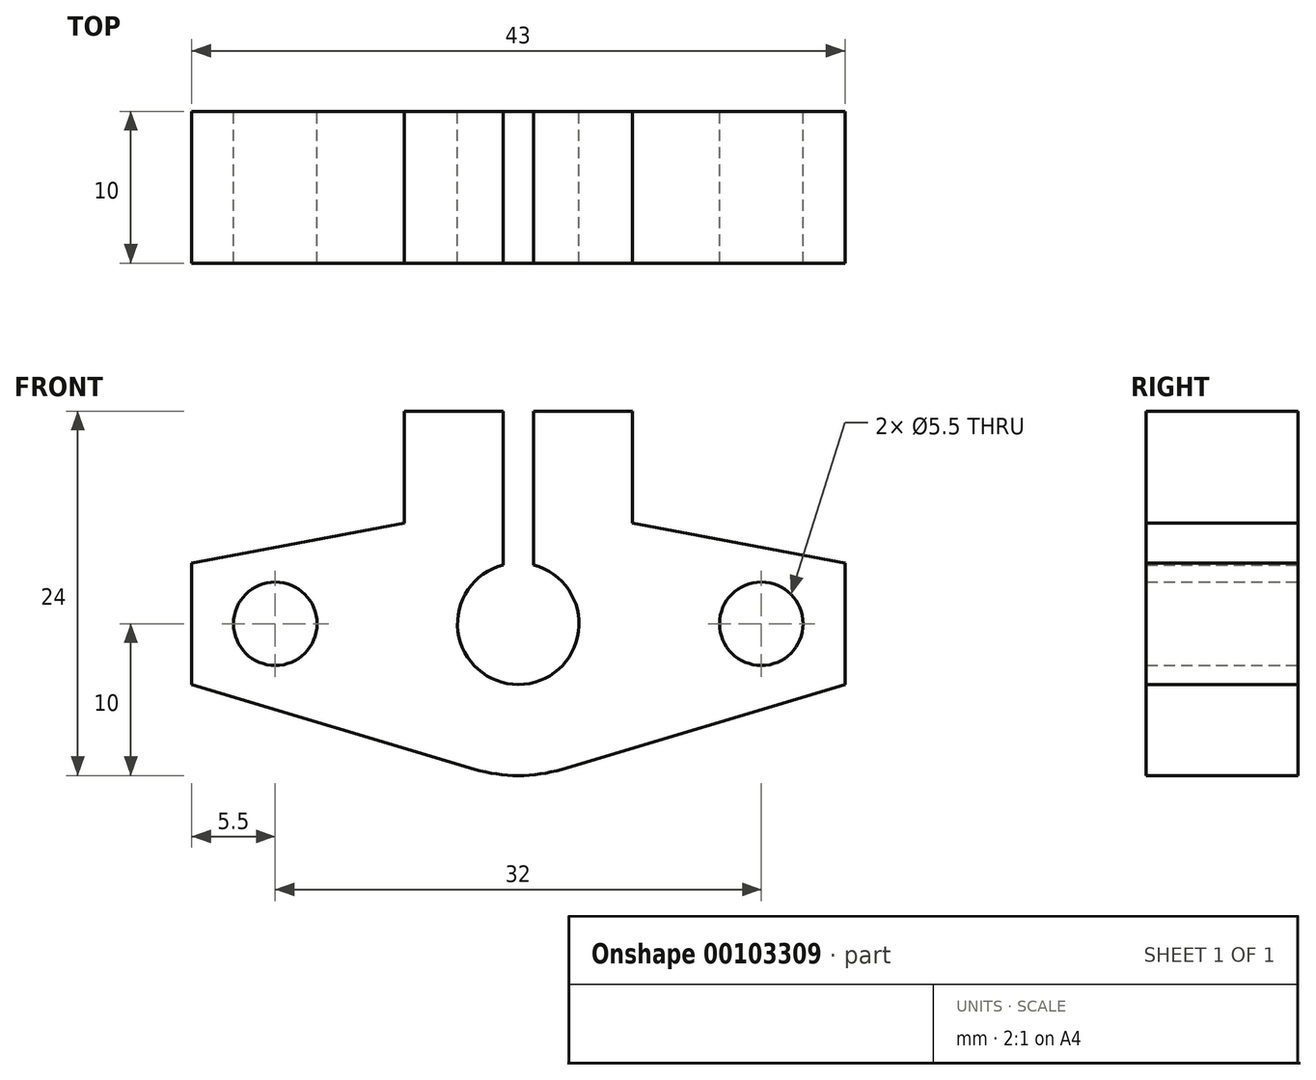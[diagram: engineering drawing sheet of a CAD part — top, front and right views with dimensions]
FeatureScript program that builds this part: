
annotation { "Feature Type Name" : "Feature", "Feature Type Description" : "" }
export const myFeature = defineFeature(function(context is Context, id is Id, definition is map)
    precondition{}
    {
        {
            var Q0;
            Q0=qCreatedBy(makeId("Front.planeOp"),FACE);
            var sketch = newSketch(context, id + "F0", { "sketchPlane" : qUnion([Q0])});
            skArc(sketch, "E0", {"start": v(-2.87, -9.58) * mm, "mid": v(0, -10) * mm, "end": v(2.87, -9.58) * mm});
            skArc(sketch, "E1", {"start": v(-1, 3.87) * mm, "mid": v(0, -4) * mm, "end": v(1, 3.87) * mm});
            skLineSegment(sketch, "E2.bottom", {"start": v(-7.5, 14) * mm, "end": v(-1, 14) * mm});
            skLineSegment(sketch, "E2.left", {"start": v(-7.5, 14) * mm, "end": v(-7.5, 6.61) * mm});
            skLineSegment(sketch, "E2.right", {"start": v(7.5, 14) * mm, "end": v(7.5, 6.61) * mm});
            skPoint(sketch, "E3", {"position": v(0, 14) * mm});
            skPoint(sketch, "E4", {"position": v(-7.5, 6.61) * mm});
            skPoint(sketch, "E5", {"position": v(7.5, 6.61) * mm});
            skPoint(sketch, "E6", {"position": v(-16, 0) * mm});
            skPoint(sketch, "E7", {"position": v(16, 0) * mm});
            skCircle(sketch, "E8", {"center": v(-16, 0) * mm, "radius": 2.75 * mm});
            skCircle(sketch, "E9", {"center": v(16, 0) * mm, "radius": 2.75 * mm});
            skLineSegment(sketch, "E10", {"start": v(-21.5, 4) * mm, "end": v(-21.5, -4) * mm});
            skLineSegment(sketch, "E11", {"start": v(-39.14, 0) * mm, "end": v(39.89, 0) * mm, "construction": true});
            skPoint(sketch, "E12", {"position": v(-21.5, 0) * mm});
            skLineSegment(sketch, "E13", {"start": v(21.5, 4) * mm, "end": v(21.5, -4) * mm});
            skPoint(sketch, "E14", {"position": v(21.5, 0) * mm});
            skLineSegment(sketch, "E15", {"start": v(-21.5, -4) * mm, "end": v(-2.87, -9.58) * mm});
            skLineSegment(sketch, "E16", {"start": v(21.5, -4) * mm, "end": v(2.87, -9.58) * mm});
            skLineSegment(sketch, "E17", {"start": v(-21.5, 4) * mm, "end": v(-7.5, 6.61) * mm});
            skLineSegment(sketch, "E18", {"start": v(21.5, 4) * mm, "end": v(7.5, 6.61) * mm});
            skLineSegment(sketch, "E19", {"start": v(-1, 14) * mm, "end": v(-1, 3.87) * mm});
            skLineSegment(sketch, "E20", {"start": v(1, 14) * mm, "end": v(1, 3.87) * mm});
            skPoint(sketch, "E21", {"position": v(-1, 14) * mm});
            skPoint(sketch, "E22", {"position": v(1, 14) * mm});
            skLineSegment(sketch, "E23.trimOffspring", {"start": v(0, 0) * mm, "end": v(0, -27.36) * mm, "construction": true});
            skLineSegment(sketch, "E24.trimOffspring", {"start": v(1, 14) * mm, "end": v(7.5, 14) * mm});
            skPoint(sketch, "E25.start.orphan", {"position": v(0, 26.83) * mm});
            skSolve(sketch);
        }
        {
            var Q0;
            Q0=makeQuery(id+"F0.imprint","IMPRINT",FACE,{"disambiguationData":[TD([[makeQuery(id+"F0.imprint","IMPRINT",EDGE,{"derivedFrom":sQuery(id+"F0.wireOp",EDGE,"E0")}),1.0]])]});
            extrude(context, id + "F1", {"entities" : qUnion([Q0]), "depth" : 10 * mm});
        }
    });
